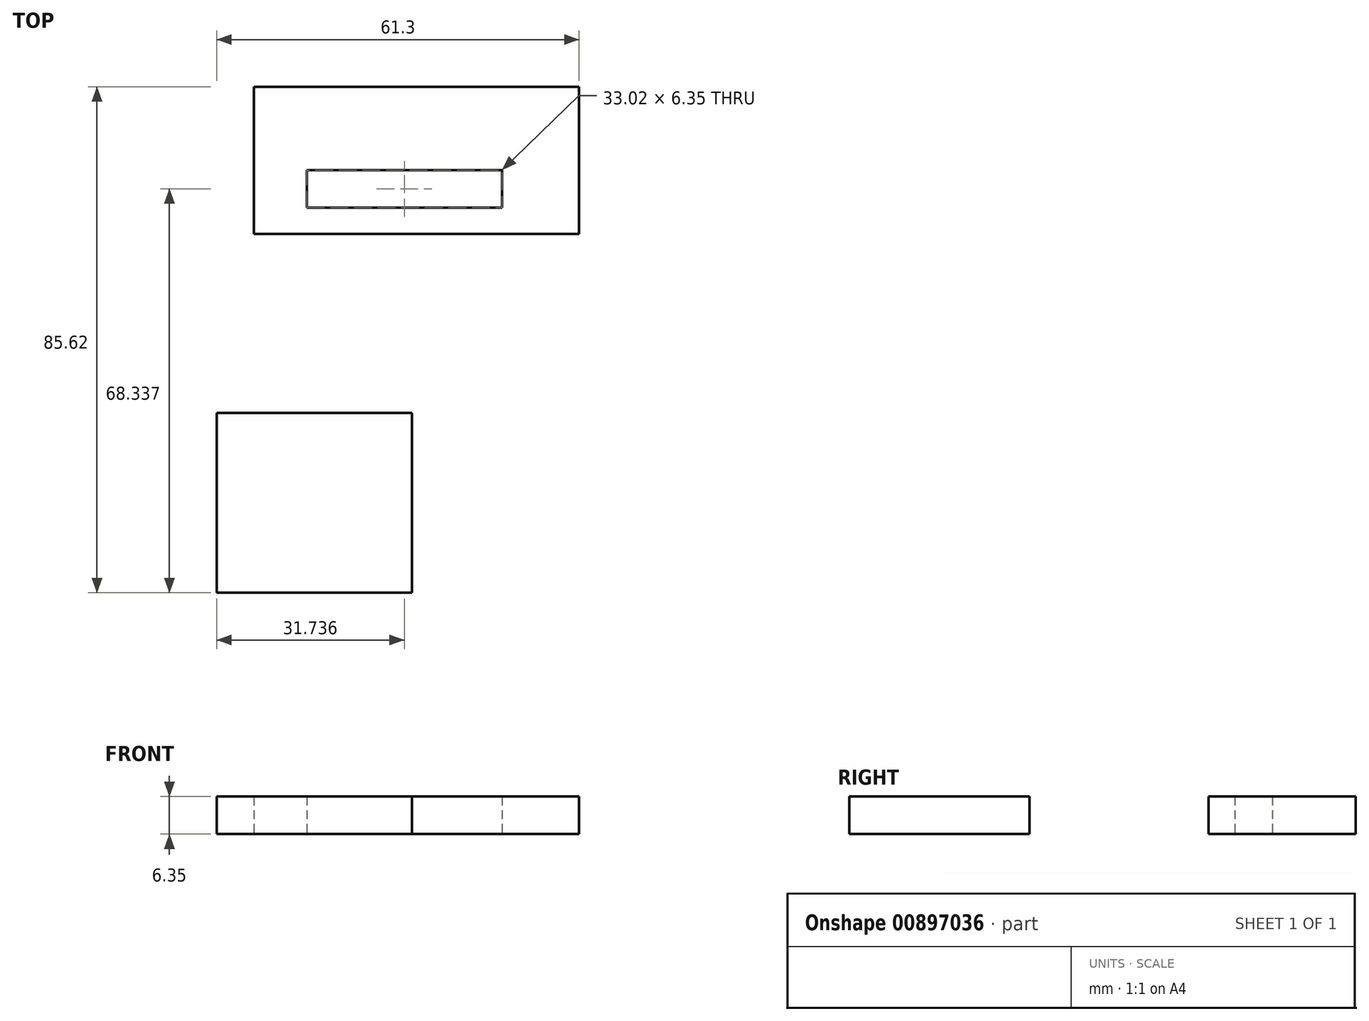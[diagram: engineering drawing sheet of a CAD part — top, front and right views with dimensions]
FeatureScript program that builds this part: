
annotation { "Feature Type Name" : "Feature", "Feature Type Description" : "" }
export const myFeature = defineFeature(function(context is Context, id is Id, definition is map)
    precondition{}
    {
        {
            var Q0;
            Q0=qCreatedBy(makeId("Top.planeOp"),FACE);
            var sketch = newSketch(context, id + "F0", { "sketchPlane" : qUnion([Q0])});
            skLineSegment(sketch, "E0.bottom", {"start": v(-19.86, 26.1) * mm, "end": v(35.15, 26.1) * mm});
            skLineSegment(sketch, "E0.top", {"start": v(-19.86, 1.21) * mm, "end": v(35.15, 1.21) * mm});
            skLineSegment(sketch, "E0.left", {"start": v(-19.86, 26.1) * mm, "end": v(-19.86, 1.21) * mm});
            skLineSegment(sketch, "E0.right", {"start": v(35.15, 26.1) * mm, "end": v(35.15, 1.21) * mm});
            skLineSegment(sketch, "E1.bottom", {"start": v(-10.92, 12) * mm, "end": v(22.1, 12) * mm});
            skLineSegment(sketch, "E1.top", {"start": v(-10.92, 5.64) * mm, "end": v(22.1, 5.64) * mm});
            skLineSegment(sketch, "E1.left", {"start": v(-10.92, 12) * mm, "end": v(-10.92, 5.64) * mm});
            skLineSegment(sketch, "E1.right", {"start": v(22.1, 12) * mm, "end": v(22.1, 5.64) * mm});
            skLineSegment(sketch, "E2.bottom", {"start": v(-26.15, -29.08) * mm, "end": v(6.87, -29.08) * mm});
            skLineSegment(sketch, "E2.left", {"start": v(-26.15, -29.08) * mm, "end": v(-26.15, -35.43) * mm});
            skLineSegment(sketch, "E2.right", {"start": v(6.87, -29.08) * mm, "end": v(6.87, -35.43) * mm});
            skLineSegment(sketch, "E3", {"start": v(-26.15, -35.43) * mm, "end": v(-26.15, -59.52) * mm});
            skLineSegment(sketch, "E4.bottom", {"start": v(-26.15, -59.52) * mm, "end": v(6.87, -59.52) * mm});
            skLineSegment(sketch, "E4.left", {"start": v(-26.15, -59.52) * mm, "end": v(-26.15, -35.43) * mm});
            skLineSegment(sketch, "E4.right", {"start": v(6.87, -59.52) * mm, "end": v(6.87, -35.43) * mm});
            skSolve(sketch);
        }
        {
            var Q0;
            Q0=makeQuery(id+"F0.imprint","IMPRINT",FACE,{"disambiguationData":[TD([[makeQuery(id+"F0.imprint","IMPRINT",EDGE,{"derivedFrom":sQuery(id+"F0.wireOp",EDGE,"E2.bottom")}),-1.0]])]});
            var Q1;
            Q1=makeQuery(id+"F0.imprint","IMPRINT",FACE,{"disambiguationData":[TD([[makeQuery(id+"F0.imprint","IMPRINT",EDGE,{"derivedFrom":sQuery(id+"F0.wireOp",EDGE,"E0.bottom")}),-1.0]])]});
            extrude(context, id + "F1", {"entities" : qUnion([Q0, Q1]), "depth" : 6.35 * mm, "offsetDistance" : 25.4 * mm});
        }
    });
